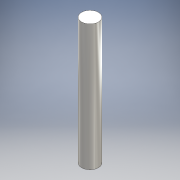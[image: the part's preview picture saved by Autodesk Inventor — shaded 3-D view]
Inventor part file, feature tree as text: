
AUTODESK INVENTOR PART (.ipt)
format: ipt  version: 2020.2 (Build 242310000, 310)  size: 90,624 bytes
history: native  units: mm
features: other x1, extrude x1, sketch x1
ambient origin geometry x8: Origin, YZ Plane, XZ Plane, XY Plane, X Axis, Y Axis, Z Axis, Center Point
bodies: Body1 (feature_tree)
feature tree (3):
  other  "ソリッド1"
  extrude  "押し出し1"  Depth=4.0mm
  sketch  "スケッチ1"
